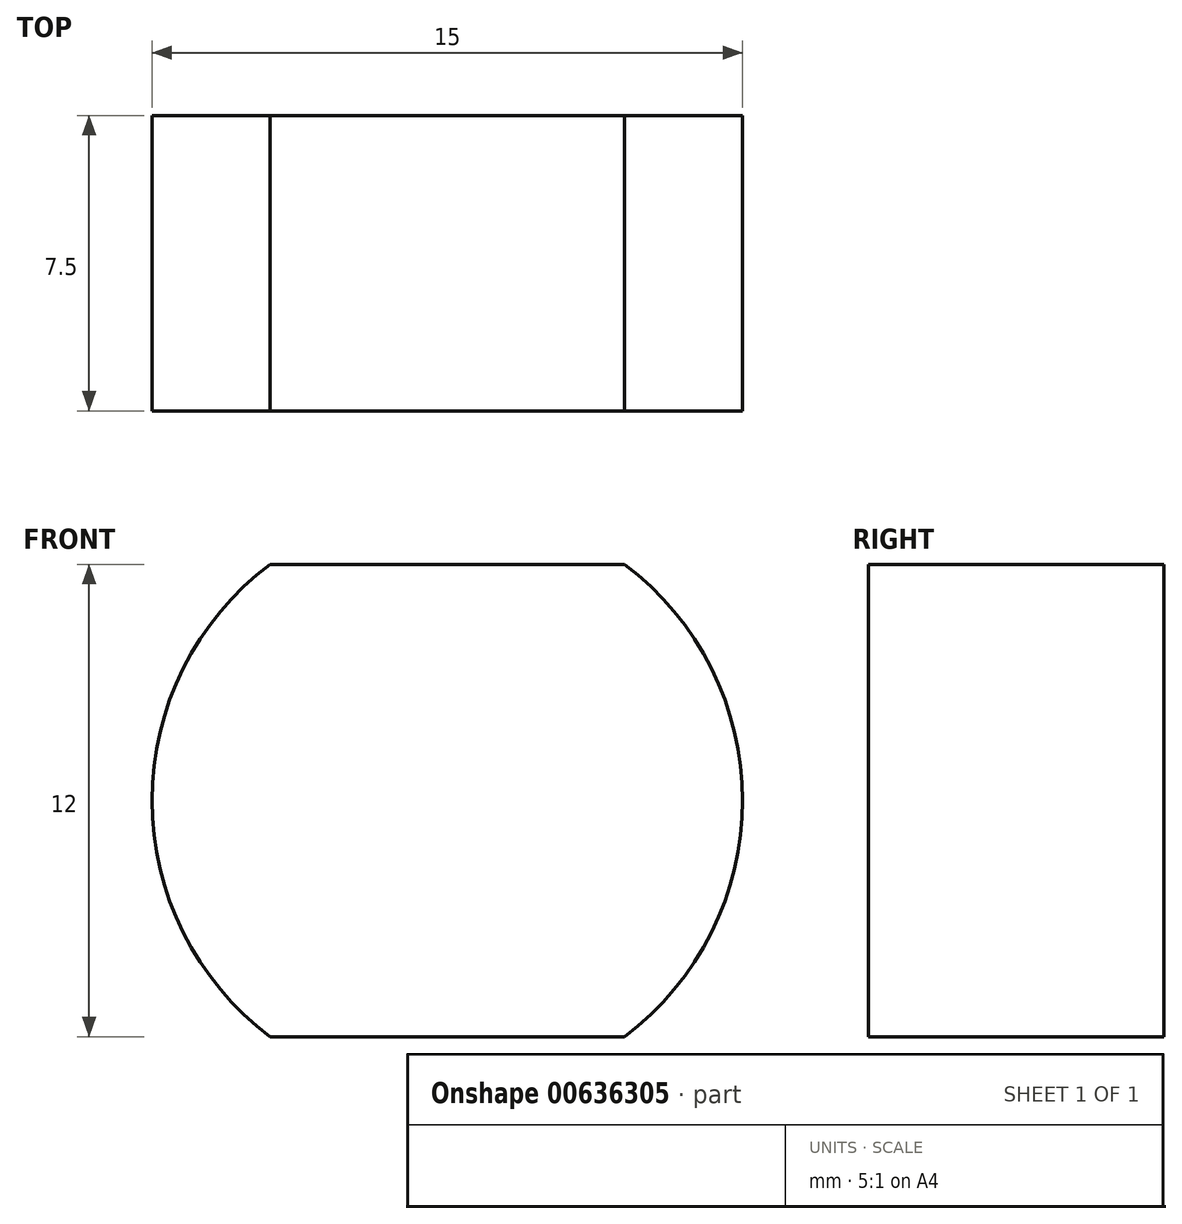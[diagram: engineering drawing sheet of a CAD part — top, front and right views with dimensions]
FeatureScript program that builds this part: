
annotation { "Feature Type Name" : "Feature", "Feature Type Description" : "" }
export const myFeature = defineFeature(function(context is Context, id is Id, definition is map)
    precondition{}
    {
        {
            var Q0;
            Q0=qCreatedBy(makeId("Front.planeOp"),FACE);
            var sketch = newSketch(context, id + "F0", { "sketchPlane" : qUnion([Q0])});
            skArc(sketch, "E0", {"start": v(-4.5, 6) * mm, "mid": v(-7.5, 0) * mm, "end": v(-4.5, -6) * mm});
            skLineSegment(sketch, "E1", {"start": v(-4.5, 6) * mm, "end": v(4.5, 6) * mm});
            skLineSegment(sketch, "E2", {"start": v(-4.5, -6) * mm, "end": v(4.5, -6) * mm});
            skArc(sketch, "E3.trimOffspring", {"start": v(4.5, -6) * mm, "mid": v(7.5, 0) * mm, "end": v(4.5, 6) * mm});
            skSolve(sketch);
        }
        {
            var Q0;
            Q0=makeQuery(id+"F0.imprint","IMPRINT",FACE,{"disambiguationData":[TD([[makeQuery(id+"F0.imprint","IMPRINT",EDGE,{"derivedFrom":sQuery(id+"F0.wireOp",EDGE,"E0")}),1.0]])]});
            extrude(context, id + "F1", {"entities" : qUnion([Q0]), "depth" : 7.5 * mm, "offsetDistance" : 25 * mm});
        }
    });
